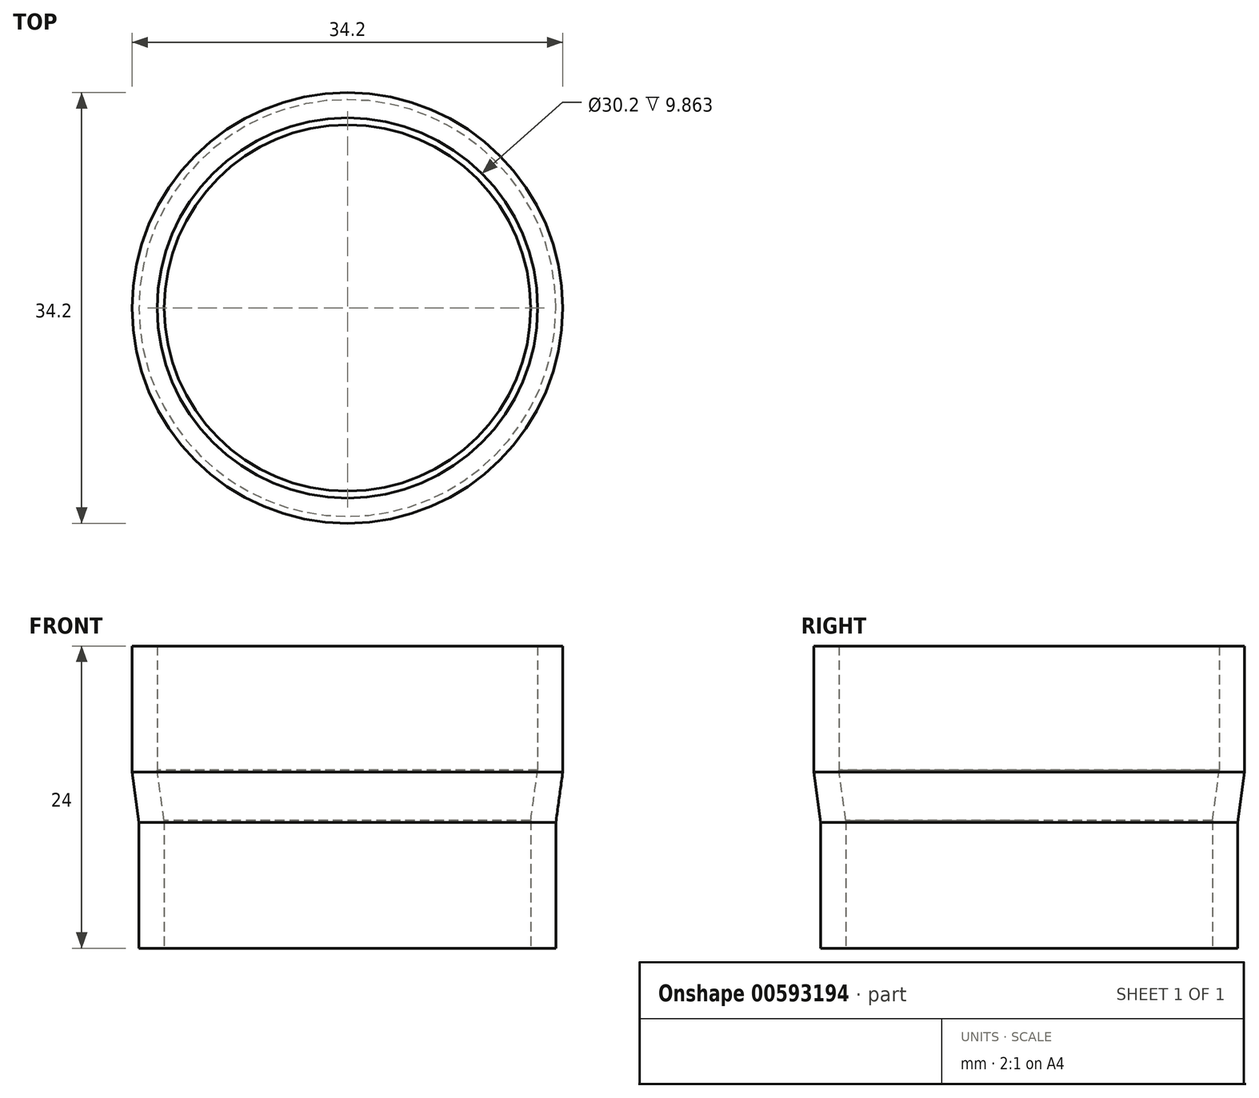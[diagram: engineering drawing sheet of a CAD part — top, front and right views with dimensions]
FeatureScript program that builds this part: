
annotation { "Feature Type Name" : "Feature", "Feature Type Description" : "" }
export const myFeature = defineFeature(function(context is Context, id is Id, definition is map)
    precondition{}
    {
        {
            var Q0;
            Q0=qCreatedBy(makeId("Top.planeOp"),FACE);
            var sketch = newSketch(context, id + "F0", { "sketchPlane" : qUnion([Q0])});
            skCircle(sketch, "E0", {"center": v(0, 0) * mm, "radius": 14.55 * mm});
            skCircle(sketch, "E1.0", {"center": v(0, 0) * mm, "radius": 16.55 * mm});
            skSolve(sketch);
        }
        {
            var Q0;
            Q0=makeQuery(id+"F0.imprint","IMPRINT",FACE,{"disambiguationData":[TD([[makeQuery(id+"F0.imprint","IMPRINT",EDGE,{"derivedFrom":sQuery(id+"F0.wireOp",EDGE,"E0")}),-1.0]])]});
            var Q1;
            Q1=makeQuery(id+"F0.imprint","IMPRINT",FACE,{"disambiguationData":[TD([[makeQuery(id+"F0.imprint","IMPRINT",EDGE,{"derivedFrom":sQuery(id+"F0.wireOp",EDGE,"E0")}),1.0]])]});
            extrude(context, id + "F1", {"entities" : qUnion([Q0, Q1]), "depth" : 10 * mm, "offsetDistance" : 25 * mm});
        }
        {
            var Q0;
            Q0=makeQuery(id+"F1.opExtrude","CAP_FACE",FACE,{"disambiguationData":[OSD([sQuery(id+"F0.wireOp",EDGE,"E0"),sQuery(id+"F0.wireOp",EDGE,"E1.0")])],"isStart":false});
            cPlane(context, id + "F2", {"entities" : qUnion([Q0]), "cplaneType" : CPlaneType.OFFSET, "offset" : 4 * mm, "width" : 150 * mm, "height" : 150 * mm});
        }
        {
            var Q0;
            Q0=qCreatedBy(id+"F2.planeOp",FACE);
            var sketch = newSketch(context, id + "F3", { "sketchPlane" : qUnion([Q0])});
            skCircle(sketch, "E2.0", {"center": v(0, 0) * mm, "radius": 17.1 * mm});
            skSolve(sketch);
        }
        {
            var Q1;
            Q1=makeQuery(id+"F1.opExtrude","CAP_FACE",FACE,{"disambiguationData":[OSD([sQuery(id+"F0.wireOp",EDGE,"E1.0")])],"isStart":false});
            var Q2;
            Q2=makeQuery(id+"F3.imprint","IMPRINT",FACE,{"disambiguationData":[TD([[makeQuery(id+"F3.imprint","IMPRINT",EDGE,{"derivedFrom":sQuery(id+"F3.wireOp",EDGE,"E2.0")}),1.0]])]});
            loft(context, id + "F4", {"operationType" : NewBodyOperationType.ADD, "sheetProfilesArray" : [{ "sheetProfileEntities" : qUnion([Q1]) }, { "sheetProfileEntities" : qUnion([Q2]) }]});
        }
        {
            var Q0;
            Q0=makeQuery(id+"F4.opLoft","CAP_FACE",FACE,{"disambiguationData":[OSD([makeQuery(id+"F3.imprint","IMPRINT",FACE,{"disambiguationData":[TD([[makeQuery(id+"F3.imprint","IMPRINT",EDGE,{"derivedFrom":sQuery(id+"F3.wireOp",EDGE,"E2.0")}),1.0]])]})])],"isStart":true});
            extrude(context, id + "F5", {"entities" : qUnion([Q0]), "operationType" : NewBodyOperationType.ADD, "depth" : 10 * mm, "offsetDistance" : 25 * mm});
        }
        {
            var Q0;
            Q0=makeQuery(id+"F5.opExtrude","CAP_FACE",FACE,{"disambiguationData":[OSD([makeQuery(id+"F3.imprint","IMPRINT",FACE,{"disambiguationData":[TD([[makeQuery(id+"F3.imprint","IMPRINT",EDGE,{"derivedFrom":sQuery(id+"F3.wireOp",EDGE,"E2.0")}),1.0]])]})])],"isStart":false});
            shell(context, id + "F6", {"entities" : qUnion([Q0]), "thickness" : 2 * mm});
        }
        {
            var Q0;
            {var subQ0=sQuery(id+"F0.wireOp",EDGE,"E1.0");Q0=makeQuery(id+"F6.opShell","OFFSET_FACE",FACE,{"disambiguationData":[OSD([subQ0]),TDD([makeQuery(id+"F1.opExtrude","CAP_FACE",FACE,{"disambiguationData":[OSD([subQ0])],"isStart":true})])]});}
            extrude(context, id + "F7", {"entities" : qUnion([Q0]), "operationType" : NewBodyOperationType.REMOVE, "oppositeDirection" : true, "depth" : 25 * mm, "offsetDistance" : 25 * mm});
        }
    });
